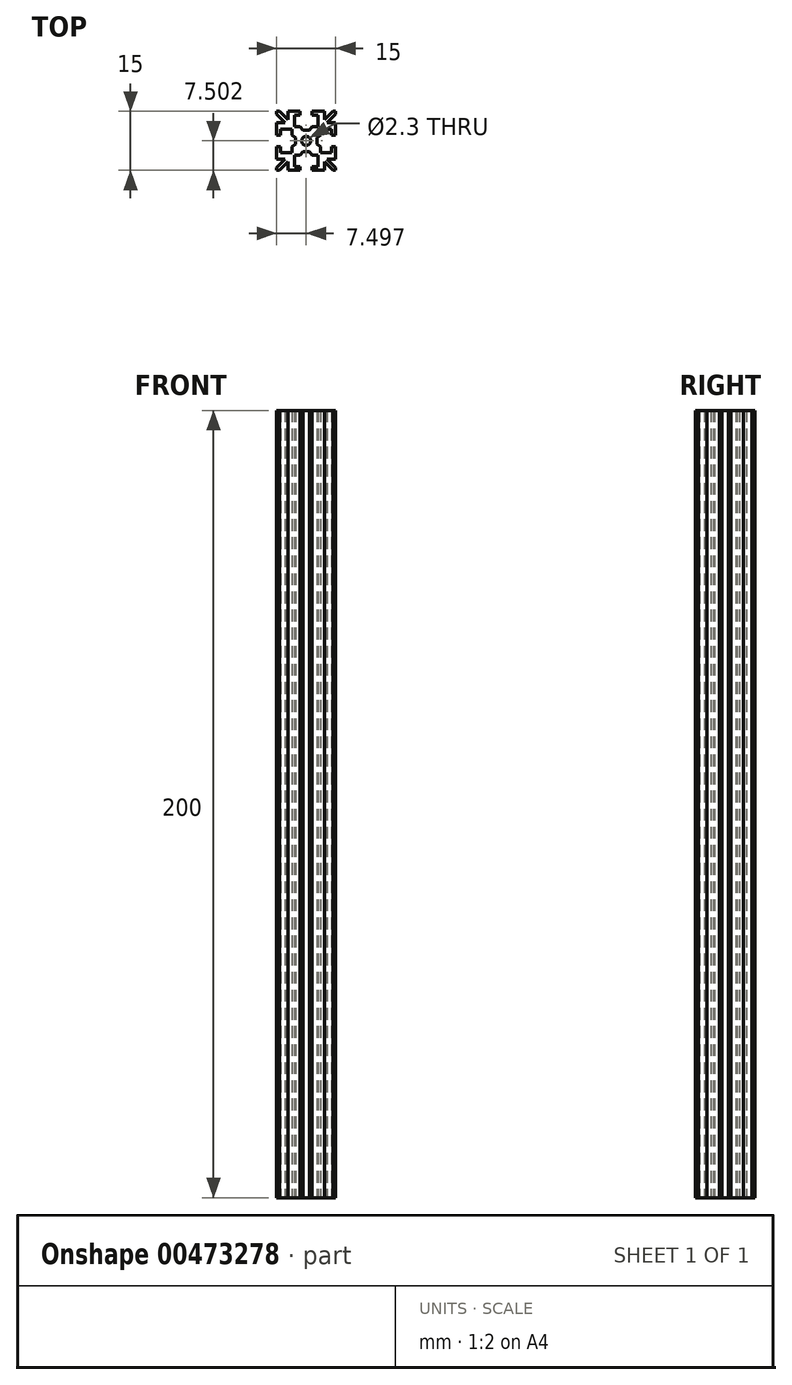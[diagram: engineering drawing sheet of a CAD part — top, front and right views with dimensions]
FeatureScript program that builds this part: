
annotation { "Feature Type Name" : "Feature", "Feature Type Description" : "" }
export const myFeature = defineFeature(function(context is Context, id is Id, definition is map)
    precondition{}
    {
        {
            var Q0;
            Q0=qCreatedBy(makeId("Top.planeOp"), FACE);
            var sketch = newSketch(context, id + "F0", { "sketchPlane" : qUnion([Q0])});
            skLineSegment(sketch, "E0", {"start": v(0.29, -0.86) * mm, "end": v(-7.21, -0.86) * mm, "construction": true});
            skLineSegment(sketch, "E1", {"start": v(-7.21, 0.64) * mm, "end": v(-7.21, 3.77) * mm});
            skLineSegment(sketch, "E2", {"start": v(0.29, 6.64) * mm, "end": v(0.29, -0.86) * mm, "construction": true});
            skArc(sketch, "E3", {"start": v(0.29, 0.3) * mm, "mid": v(-0.53, -0.04) * mm, "end": v(-0.86, -0.86) * mm});
            skLineSegment(sketch, "E4", {"start": v(0.29, -0.86) * mm, "end": v(-7.21, 6.64) * mm, "construction": true});
            skLineSegment(sketch, "E5.top", {"start": v(-7.21, 0.64) * mm, "end": v(-6.21, 0.64) * mm});
            skLineSegment(sketch, "E5.left", {"start": v(-7.21, 6.64) * mm, "end": v(-7.21, 5.94) * mm});
            skLineSegment(sketch, "E6", {"start": v(-6.21, 0.64) * mm, "end": v(-6.21, 2.14) * mm});
            skLineSegment(sketch, "E7", {"start": v(-6.21, 2.14) * mm, "end": v(-3.36, 2.14) * mm});
            skLineSegment(sketch, "E8", {"start": v(-3.36, 2.14) * mm, "end": v(-3.36, 0.64) * mm});
            skLineSegment(sketch, "E9", {"start": v(-3.36, 0.64) * mm, "end": v(-2.43, -0.04) * mm});
            skLineSegment(sketch, "E10", {"start": v(-2.43, -0.04) * mm, "end": v(-2.43, -0.86) * mm});
            skLineSegment(sketch, "E11", {"start": v(-7.21, 5.94) * mm, "end": v(-5.05, 3.77) * mm});
            skLineSegment(sketch, "E12", {"start": v(-5.05, 3.77) * mm, "end": v(-7.21, 3.77) * mm});
            skLineSegment(sketch, "E13.trimOffspring", {"start": v(-7.21, 3.77) * mm, "end": v(-7.21, 0.64) * mm});
            skLineSegment(sketch, "E14.trimOffspring", {"start": v(-7.21, 5.94) * mm, "end": v(-7.21, 6.64) * mm});
            skLineSegment(sketch, "E15.MirrorCS", {"start": v(-1.21, 6.64) * mm, "end": v(-4.34, 6.64) * mm});
            skLineSegment(sketch, "E16.MirrorCS", {"start": v(-7.21, 6.64) * mm, "end": v(-6.5, 6.64) * mm});
            skLineSegment(sketch, "E17.MirrorCS", {"start": v(-6.5, 6.64) * mm, "end": v(-7.21, 6.64) * mm});
            skLineSegment(sketch, "E18.MirrorCS", {"start": v(-4.34, 6.64) * mm, "end": v(-1.21, 6.64) * mm});
            skLineSegment(sketch, "E19.MirrorCS", {"start": v(-6.5, 6.64) * mm, "end": v(-4.34, 4.48) * mm});
            skLineSegment(sketch, "E20.MirrorCS", {"start": v(-2.71, 2.8) * mm, "end": v(-1.21, 2.8) * mm});
            skLineSegment(sketch, "E21.MirrorCS", {"start": v(-1.21, 2.8) * mm, "end": v(-0.53, 1.86) * mm});
            skLineSegment(sketch, "E22.MirrorCS", {"start": v(-2.71, 5.64) * mm, "end": v(-2.71, 2.8) * mm});
            skLineSegment(sketch, "E23.MirrorCS", {"start": v(-1.21, 6.64) * mm, "end": v(-1.21, 5.64) * mm});
            skLineSegment(sketch, "E24.MirrorCS", {"start": v(-1.21, 5.64) * mm, "end": v(-2.71, 5.64) * mm});
            skLineSegment(sketch, "E25.MirrorCS", {"start": v(-4.34, 4.48) * mm, "end": v(-4.34, 6.64) * mm});
            skLineSegment(sketch, "E26.MirrorCS", {"start": v(-0.53, 1.86) * mm, "end": v(0.29, 1.86) * mm});
            skLineSegment(sketch, "E27.MirrorCS", {"start": v(7.79, 3.77) * mm, "end": v(7.79, 0.64) * mm});
            skLineSegment(sketch, "E28.MirrorCS", {"start": v(7.79, 5.94) * mm, "end": v(7.79, 6.64) * mm});
            skLineSegment(sketch, "E29.MirrorCS", {"start": v(7.79, 6.64) * mm, "end": v(7.08, 6.64) * mm});
            skLineSegment(sketch, "E30.MirrorCS", {"start": v(4.92, 6.64) * mm, "end": v(1.79, 6.64) * mm});
            skLineSegment(sketch, "E31.MirrorCS", {"start": v(1.79, 6.64) * mm, "end": v(4.92, 6.64) * mm});
            skLineSegment(sketch, "E32.MirrorCS", {"start": v(7.08, 6.64) * mm, "end": v(7.79, 6.64) * mm});
            skLineSegment(sketch, "E33.MirrorCS", {"start": v(7.08, 6.64) * mm, "end": v(4.92, 4.48) * mm});
            skLineSegment(sketch, "E34.MirrorCS", {"start": v(1.79, 2.8) * mm, "end": v(1.1, 1.86) * mm});
            skLineSegment(sketch, "E35.MirrorCS", {"start": v(3.29, 5.64) * mm, "end": v(3.29, 2.8) * mm});
            skLineSegment(sketch, "E36.MirrorCS", {"start": v(1.79, 5.64) * mm, "end": v(3.29, 5.64) * mm});
            skLineSegment(sketch, "E37.MirrorCS", {"start": v(1.1, 1.86) * mm, "end": v(0.29, 1.86) * mm});
            skLineSegment(sketch, "E38.MirrorCS", {"start": v(7.79, 5.94) * mm, "end": v(5.62, 3.77) * mm});
            skLineSegment(sketch, "E39.MirrorCS", {"start": v(3, -0.04) * mm, "end": v(3, -0.86) * mm});
            skLineSegment(sketch, "E40.MirrorCS", {"start": v(3.94, 0.64) * mm, "end": v(3, -0.04) * mm});
            skLineSegment(sketch, "E41.MirrorCS", {"start": v(3.94, 2.14) * mm, "end": v(3.94, 0.64) * mm});
            skLineSegment(sketch, "E42.MirrorCS", {"start": v(6.79, 2.14) * mm, "end": v(3.94, 2.14) * mm});
            skLineSegment(sketch, "E43.MirrorCS", {"start": v(6.79, 0.64) * mm, "end": v(6.79, 2.14) * mm});
            skLineSegment(sketch, "E44.MirrorCS", {"start": v(7.79, 6.64) * mm, "end": v(7.79, 5.94) * mm});
            skLineSegment(sketch, "E45.MirrorCS", {"start": v(7.79, 0.64) * mm, "end": v(6.79, 0.64) * mm});
            skLineSegment(sketch, "E46.MirrorCS", {"start": v(0.29, -0.86) * mm, "end": v(7.79, 6.64) * mm, "construction": true});
            skLineSegment(sketch, "E47.MirrorCS", {"start": v(7.79, 0.64) * mm, "end": v(7.79, 3.77) * mm});
            skArc(sketch, "E48.MirrorCS", {"start": v(0.29, 0.3) * mm, "mid": v(1.1, -0.04) * mm, "end": v(1.44, -0.86) * mm});
            skLineSegment(sketch, "E49.MirrorCS", {"start": v(0.29, -0.86) * mm, "end": v(7.79, -0.86) * mm, "construction": true});
            skLineSegment(sketch, "E50.MirrorCS", {"start": v(5.62, 3.77) * mm, "end": v(7.79, 3.77) * mm});
            skLineSegment(sketch, "E51.MirrorCS", {"start": v(4.92, 4.48) * mm, "end": v(4.92, 6.64) * mm});
            skLineSegment(sketch, "E52.MirrorCS", {"start": v(1.79, 6.64) * mm, "end": v(1.79, 5.64) * mm});
            skLineSegment(sketch, "E53.MirrorCS", {"start": v(3.29, 2.8) * mm, "end": v(1.79, 2.8) * mm});
            skLineSegment(sketch, "E54.MirrorCS", {"start": v(-4.34, -8.36) * mm, "end": v(-1.21, -8.36) * mm});
            skLineSegment(sketch, "E55.MirrorCS", {"start": v(1.79, -4.5) * mm, "end": v(1.1, -3.57) * mm});
            skLineSegment(sketch, "E56.MirrorCS", {"start": v(-7.21, -5.49) * mm, "end": v(-7.21, -2.36) * mm});
            skLineSegment(sketch, "E57.MirrorCS", {"start": v(-7.21, -7.65) * mm, "end": v(-7.21, -8.36) * mm});
            skLineSegment(sketch, "E58.MirrorCS", {"start": v(7.79, -8.36) * mm, "end": v(7.79, -7.65) * mm});
            skLineSegment(sketch, "E59.MirrorCS", {"start": v(-7.21, -8.36) * mm, "end": v(-6.5, -8.36) * mm});
            skLineSegment(sketch, "E60.MirrorCS", {"start": v(7.79, -8.36) * mm, "end": v(7.08, -8.36) * mm});
            skLineSegment(sketch, "E61.MirrorCS", {"start": v(1.79, -8.36) * mm, "end": v(4.92, -8.36) * mm});
            skLineSegment(sketch, "E62.MirrorCS", {"start": v(7.79, -2.36) * mm, "end": v(7.79, -5.49) * mm});
            skLineSegment(sketch, "E63.MirrorCS", {"start": v(3.94, -3.86) * mm, "end": v(3.94, -2.36) * mm});
            skLineSegment(sketch, "E64.MirrorCS", {"start": v(-4.34, -6.2) * mm, "end": v(-4.34, -8.36) * mm});
            skLineSegment(sketch, "E65.MirrorCS", {"start": v(5.62, -5.49) * mm, "end": v(7.79, -5.49) * mm});
            skLineSegment(sketch, "E66.MirrorCS", {"start": v(-5.05, -5.49) * mm, "end": v(-7.21, -5.49) * mm});
            skLineSegment(sketch, "E67.MirrorCS", {"start": v(-7.21, -2.36) * mm, "end": v(-7.21, -5.49) * mm});
            skLineSegment(sketch, "E68.MirrorCS", {"start": v(0.29, -8.36) * mm, "end": v(0.29, -0.86) * mm, "construction": true});
            skArc(sketch, "E69.MirrorCS", {"start": v(0.29, -2) * mm, "mid": v(-0.53, -1.67) * mm, "end": v(-0.86, -0.86) * mm});
            skLineSegment(sketch, "E70.MirrorCS", {"start": v(0.29, -0.86) * mm, "end": v(-7.21, -8.36) * mm, "construction": true});
            skLineSegment(sketch, "E71.MirrorCS", {"start": v(-7.21, -2.36) * mm, "end": v(-6.21, -2.36) * mm});
            skLineSegment(sketch, "E72.MirrorCS", {"start": v(-7.21, -8.36) * mm, "end": v(-7.21, -7.65) * mm});
            skLineSegment(sketch, "E73.MirrorCS", {"start": v(-6.21, -2.36) * mm, "end": v(-6.21, -3.86) * mm});
            skLineSegment(sketch, "E74.MirrorCS", {"start": v(-6.21, -3.86) * mm, "end": v(-3.36, -3.86) * mm});
            skLineSegment(sketch, "E75.MirrorCS", {"start": v(-3.36, -3.86) * mm, "end": v(-3.36, -2.36) * mm});
            skLineSegment(sketch, "E76.MirrorCS", {"start": v(-3.36, -2.36) * mm, "end": v(-2.43, -1.67) * mm});
            skLineSegment(sketch, "E77.MirrorCS", {"start": v(-2.43, -1.67) * mm, "end": v(-2.43, -0.86) * mm});
            skLineSegment(sketch, "E78.MirrorCS", {"start": v(-7.21, -7.65) * mm, "end": v(-5.05, -5.49) * mm});
            skLineSegment(sketch, "E79.MirrorCS", {"start": v(6.79, -3.86) * mm, "end": v(3.94, -3.86) * mm});
            skLineSegment(sketch, "E80.MirrorCS", {"start": v(-0.53, -3.57) * mm, "end": v(0.29, -3.57) * mm});
            skLineSegment(sketch, "E81.MirrorCS", {"start": v(7.79, -7.65) * mm, "end": v(5.62, -5.49) * mm});
            skLineSegment(sketch, "E82.MirrorCS", {"start": v(-2.71, -7.36) * mm, "end": v(-2.71, -4.5) * mm});
            skLineSegment(sketch, "E83.MirrorCS", {"start": v(-6.5, -8.36) * mm, "end": v(-4.34, -6.2) * mm});
            skLineSegment(sketch, "E84.MirrorCS", {"start": v(4.92, -6.2) * mm, "end": v(4.92, -8.36) * mm});
            skLineSegment(sketch, "E85.MirrorCS", {"start": v(7.79, -7.65) * mm, "end": v(7.79, -8.36) * mm});
            skLineSegment(sketch, "E86.MirrorCS", {"start": v(3.29, -7.36) * mm, "end": v(3.29, -4.5) * mm});
            skLineSegment(sketch, "E87.MirrorCS", {"start": v(-1.21, -8.36) * mm, "end": v(-4.34, -8.36) * mm});
            skLineSegment(sketch, "E88.MirrorCS", {"start": v(7.08, -8.36) * mm, "end": v(4.92, -6.2) * mm});
            skLineSegment(sketch, "E89.MirrorCS", {"start": v(7.08, -8.36) * mm, "end": v(7.79, -8.36) * mm});
            skLineSegment(sketch, "E90.MirrorCS", {"start": v(0.29, -0.86) * mm, "end": v(7.79, -8.36) * mm, "construction": true});
            skArc(sketch, "E91.MirrorCS", {"start": v(0.29, -2) * mm, "mid": v(1.1, -1.67) * mm, "end": v(1.44, -0.86) * mm});
            skLineSegment(sketch, "E92.MirrorCS", {"start": v(1.79, -7.36) * mm, "end": v(3.29, -7.36) * mm});
            skLineSegment(sketch, "E93.MirrorCS", {"start": v(7.79, -2.36) * mm, "end": v(6.79, -2.36) * mm});
            skLineSegment(sketch, "E94.MirrorCS", {"start": v(1.79, -8.36) * mm, "end": v(1.79, -7.36) * mm});
            skLineSegment(sketch, "E95.MirrorCS", {"start": v(-2.71, -4.5) * mm, "end": v(-1.21, -4.5) * mm});
            skLineSegment(sketch, "E96.MirrorCS", {"start": v(-1.21, -8.36) * mm, "end": v(-1.21, -7.36) * mm});
            skLineSegment(sketch, "E97.MirrorCS", {"start": v(3, -1.67) * mm, "end": v(3, -0.86) * mm});
            skLineSegment(sketch, "E98.MirrorCS", {"start": v(7.79, -5.49) * mm, "end": v(7.79, -2.36) * mm});
            skLineSegment(sketch, "E99.MirrorCS", {"start": v(6.79, -2.36) * mm, "end": v(6.79, -3.86) * mm});
            skLineSegment(sketch, "E100.MirrorCS", {"start": v(-6.5, -8.36) * mm, "end": v(-7.21, -8.36) * mm});
            skLineSegment(sketch, "E101.MirrorCS", {"start": v(3.29, -4.5) * mm, "end": v(1.79, -4.5) * mm});
            skLineSegment(sketch, "E102.MirrorCS", {"start": v(4.92, -8.36) * mm, "end": v(1.79, -8.36) * mm});
            skLineSegment(sketch, "E103.MirrorCS", {"start": v(-1.21, -7.36) * mm, "end": v(-2.71, -7.36) * mm});
            skLineSegment(sketch, "E104.MirrorCS", {"start": v(3.94, -2.36) * mm, "end": v(3, -1.67) * mm});
            skLineSegment(sketch, "E105.MirrorCS", {"start": v(1.1, -3.57) * mm, "end": v(0.29, -3.57) * mm});
            skLineSegment(sketch, "E106.MirrorCS", {"start": v(-1.21, -4.5) * mm, "end": v(-0.53, -3.57) * mm});
            skSolve(sketch);
        }
        {
            var Q0;
            Q0 = qSketchRegion(id + "F0", true);
            extrude(context, id + "F1", {"entities" : qUnion([Q0]), "depth" : 200 * mm, "offsetDistance" : 25 * mm});
        }
    });
